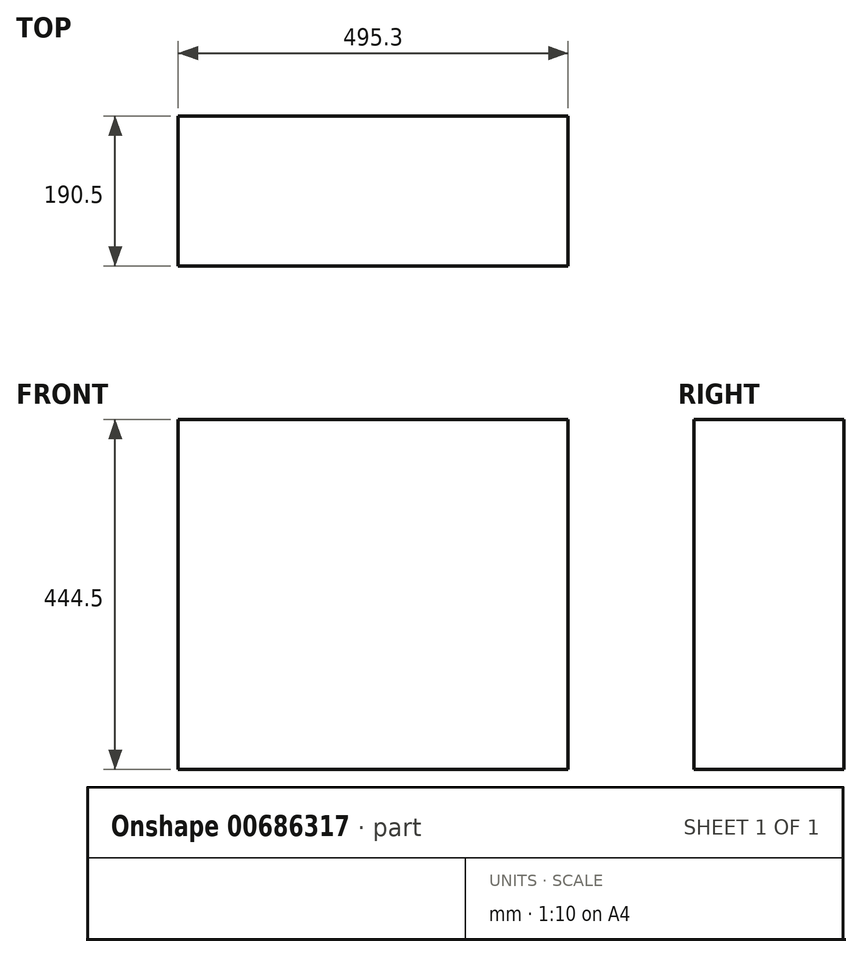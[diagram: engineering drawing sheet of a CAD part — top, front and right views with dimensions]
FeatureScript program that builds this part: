
annotation { "Feature Type Name" : "Feature", "Feature Type Description" : "" }
export const myFeature = defineFeature(function(context is Context, id is Id, definition is map)
    precondition{}
    {
        {
            var Q0;
            Q0=qCreatedBy(makeId("Right.planeOp"),FACE);
            var sketch = newSketch(context, id + "F0", { "sketchPlane" : qUnion([Q0])});
            skLineSegment(sketch, "E0.bottom", {"start": v(95.25, 222.25) * mm, "end": v(-95.25, 222.25) * mm});
            skLineSegment(sketch, "E0.top", {"start": v(95.25, -222.25) * mm, "end": v(-95.25, -222.25) * mm});
            skLineSegment(sketch, "E0.left", {"start": v(95.25, 222.25) * mm, "end": v(95.25, -222.25) * mm});
            skLineSegment(sketch, "E0.right", {"start": v(-95.25, 222.25) * mm, "end": v(-95.25, -222.25) * mm});
            skPoint(sketch, "E0.middle", {"position": v(0, 0) * mm});
            skSolve(sketch);
        }
        {
            var Q0;
            Q0 = qSketchRegion(id + "F0", true);
            extrude(context, id + "F1", {"entities" : qUnion([Q0]), "endBound" : BoundingType.SYMMETRIC, "depth" : 495.3 * mm, "offsetDistance" : 25.4 * mm});
        }
    });
